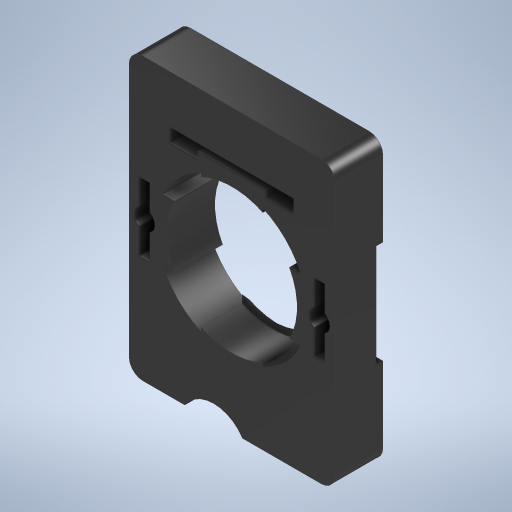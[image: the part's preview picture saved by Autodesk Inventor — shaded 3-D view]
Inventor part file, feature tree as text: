
AUTODESK INVENTOR PART (.ipt)
format: ipt  version: 2023 (Build 270158000, 158)  size: 563,712 bytes
history: native  units: mm
features: extrude x12, sketch x12, fillet x3, other x1, chamfer x1
ambient origin geometry x8: Origin, YZ Plane, XZ Plane, XY Plane, X Axis, Y Axis, Z Axis, Center Point
bodies: Body1 (feature_tree)
feature tree (29):
  other  "Sólido1"
  extrude  "Extrusão1"  Depth=30.0mm
  extrude  "Extrusão2"  Depth=22.0mm
  extrude  "Extrusão3"  Depth=10.0mm
  extrude  "Extrusão4"  Depth=1.5mm
  extrude  "Extrusão5"  Depth=1.5mm
  extrude  "Extrusão6"  Depth=1.5mm
  extrude  "Extrusão7"  TaperAngle=0.0deg  [1 undecoded]
  chamfer  "Chanfro1"  [1 undecoded]
  extrude  "Extrusão8"  Depth=22.0mm
  fillet  "Arredondamento1"  Radius=30.0mm
  extrude  "Extrusão9"  Depth=9.0mm
  extrude  "Extrusão10"  Depth=9.0mm
  extrude  "Extrusão11"  Depth=30.0mm
  extrude  "Extrusão12"  Depth=7.0mm TaperAngle=0.0deg
  fillet  "Arredondamento2"  Radius=22.0mm
  fillet  "Arredondamento3"  Radius=21.0mm
  sketch  "Esboço1"  dims[d0=30.0mm d1=41.0mm]
  sketch  "Esboço2"  dims[d2=7.0mm d3=0.0mm d4=22.0mm]
  sketch  "Esboço3"  dims[d5=7.0mm d6=0.0mm d7=10.0mm]
  sketch  "Esboço5"  dims[d8=0.0mm d9=0.0mm d10=1.5mm]
  sketch  "Esboço6"  dims[d11=10.0mm d12=1.5mm]
  sketch  "Esboço7"  dims[d13=10.0mm d14=1.5mm]
  sketch  "Esboço8"  dims[d15=1.5mm d16=0.0mm d17=0.0mm]
  sketch  "Esboço9"  dims[d18=3.0mm]
  sketch  "Esboço10"  dims[d19=3.0mm]
  sketch  "Esboço11"  dims[d20=0.0mm]
  sketch  "Esboço12"  dims[d21=0.0mm d22=0.0mm d23=0.0mm]
  sketch  "Esboço13"  dims[d24=19.0mm d25=22.0mm d26=30.0mm d27=9.0mm d28=9.0mm d29=30.0mm d30=7.0mm d31=0.0mm d32=22.0mm d33=21.0mm d34=19.0mm d35=9.0mm d36=30.0mm d37=30.0mm d38=9.0mm d39=6.0mm d40=0.0mm d41=1.0mm d42=2.0mm d43=45.0deg d44=5.0mm d45=15.0mm d46=5.0mm d47=15.0mm d48=1.0mm d49=0.0mm d50=2.0mm d51=18.0mm d52=1.0mm d53=2.0mm d54=0.0mm d55=0.0mm d56=4.0mm d57=1.0mm d58=4.0mm d59=1.0mm d60=0.0mm d61=0.0mm d62=0.0mm d63=0.0mm d64=10.0mm d65=0.0mm d66=6.0mm d67=5.0mm d68=7.0mm d69=7.0mm d70=7.0mm d71=7.0mm d72=2.0mm d73=6.0mm d74=2.0mm d75=6.0mm d76=1.0mm d77=1.0mm d78=5.5mm d79=5.5mm d80=6.0mm d81=0.0mm d82=7.0mm d83=5.0mm d84=5.0mm d85=5.0mm d86=5.0mm d87=5.0mm d88=2.0mm d89=10.0mm d90=2.0mm d91=10.0mm d92=7.5mm d93=7.5mm d94=5.0mm d95=5.0mm d96=6.0mm d97=0.0mm d98=1.0mm d99=1.0mm]
note: 2 required parameter values undecoded (feature->parameter linkage not recoverable at this tier; creation-order binding heuristic only, values carry confidence <= 0.55)
